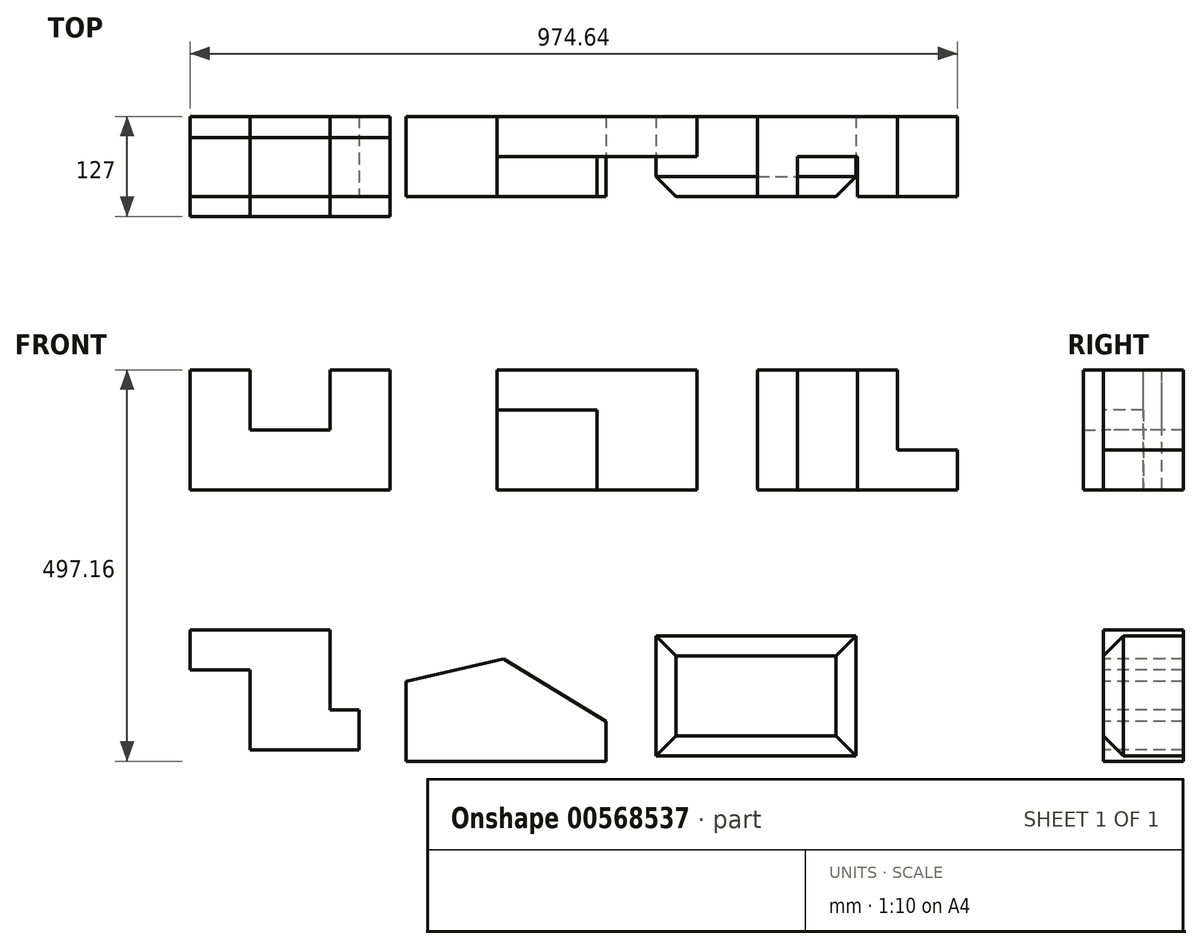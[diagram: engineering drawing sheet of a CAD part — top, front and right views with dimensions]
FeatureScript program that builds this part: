
annotation { "Feature Type Name" : "Feature", "Feature Type Description" : "" }
export const myFeature = defineFeature(function(context is Context, id is Id, definition is map)
    precondition{}
    {
        {
            var Q0;
            Q0=qCreatedBy(makeId("Front.planeOp"),FACE);
            var sketch = newSketch(context, id + "F0", { "sketchPlane" : qUnion([Q0])});
            skLineSegment(sketch, "E0", {"start": v(0, 0) * mm, "end": v(0, 152.4) * mm});
            skLineSegment(sketch, "E1", {"start": v(0, 152.4) * mm, "end": v(76.2, 152.4) * mm});
            skLineSegment(sketch, "E2", {"start": v(76.2, 152.4) * mm, "end": v(76.2, 76.2) * mm});
            skLineSegment(sketch, "E3", {"start": v(76.2, 76.2) * mm, "end": v(177.8, 76.2) * mm});
            skLineSegment(sketch, "E4", {"start": v(177.8, 76.2) * mm, "end": v(177.8, 152.4) * mm});
            skLineSegment(sketch, "E5", {"start": v(177.8, 152.4) * mm, "end": v(254, 152.4) * mm});
            skLineSegment(sketch, "E6", {"start": v(254, 152.4) * mm, "end": v(254, 0) * mm});
            skLineSegment(sketch, "E7", {"start": v(254, 0) * mm, "end": v(0, 0) * mm});
            skSolve(sketch);
        }
        {
            var Q0;
            Q0=makeQuery(id+"F0.imprint","IMPRINT",FACE,{"disambiguationData":[TD([[makeQuery(id+"F0.imprint","IMPRINT",EDGE,{"derivedFrom":sQuery(id+"F0.wireOp",EDGE,"E0")}),-1.0]])]});
            extrude(context, id + "F1", {"entities" : qUnion([Q0]), "oppositeDirection" : true, "depth" : 101.6 * mm, "offsetDistance" : 25.4 * mm});
        }
        {
            var Q0;
            Q0=qCreatedBy(makeId("Front.planeOp"),FACE);
            var sketch = newSketch(context, id + "F2", { "sketchPlane" : qUnion([Q0])});
            skLineSegment(sketch, "E8.bottom", {"start": v(390.09, 0) * mm, "end": v(644.09, 0) * mm});
            skLineSegment(sketch, "E8.top", {"start": v(390.09, 152.4) * mm, "end": v(644.09, 152.4) * mm});
            skLineSegment(sketch, "E8.left", {"start": v(390.09, 0) * mm, "end": v(390.09, 152.4) * mm});
            skLineSegment(sketch, "E8.right", {"start": v(644.09, 0) * mm, "end": v(644.09, 152.4) * mm});
            skSolve(sketch);
        }
        {
            var Q0;
            Q0=makeQuery(id+"F2.imprint","IMPRINT",FACE,{"disambiguationData":[TD([[makeQuery(id+"F2.imprint","IMPRINT",EDGE,{"derivedFrom":sQuery(id+"F2.wireOp",EDGE,"E8.bottom")}),1.0]])]});
            extrude(context, id + "F3", {"entities" : qUnion([Q0]), "oppositeDirection" : true, "depth" : 101.6 * mm, "offsetDistance" : 25.4 * mm});
        }
        {
            var Q0;
            Q0=makeQuery(id+"F3.opExtrude","CAP_FACE",FACE,{"disambiguationData":[OSD([sQuery(id+"F2.wireOp",EDGE,"E8.bottom"),sQuery(id+"F2.wireOp",EDGE,"E8.top"),sQuery(id+"F2.wireOp",EDGE,"E8.left"),sQuery(id+"F2.wireOp",EDGE,"E8.right")])],"isStart":true});
            var sketch = newSketch(context, id + "F4", { "sketchPlane" : qUnion([Q0])});
            skLineSegment(sketch, "E9", {"start": v(390.09, 152.4) * mm, "end": v(390.09, 101.6) * mm});
            skLineSegment(sketch, "E10", {"start": v(390.09, 101.6) * mm, "end": v(517.09, 101.6) * mm});
            skLineSegment(sketch, "E11", {"start": v(517.09, 101.6) * mm, "end": v(517.09, 0) * mm});
            skLineSegment(sketch, "E12", {"start": v(517.09, 0) * mm, "end": v(644.09, 0) * mm});
            skLineSegment(sketch, "E13", {"start": v(644.09, 0) * mm, "end": v(644.09, 152.4) * mm});
            skLineSegment(sketch, "E14", {"start": v(644.09, 152.4) * mm, "end": v(390.09, 152.4) * mm});
            skSolve(sketch);
        }
        {
            var Q0;
            Q0=makeQuery(id+"F4.imprint","IMPRINT",FACE,{"disambiguationData":[TD([[makeQuery(id+"F4.imprint","IMPRINT",EDGE,{"derivedFrom":sQuery(id+"F4.wireOp",EDGE,"E9")}),-1.0]])]});
            extrude(context, id + "F5", {"entities" : qUnion([Q0]), "operationType" : NewBodyOperationType.REMOVE, "oppositeDirection" : true, "depth" : 50.8 * mm, "offsetDistance" : 25.4 * mm});
        }
        {
            var Q0;
            Q0=qCreatedBy(makeId("Front.planeOp"),FACE);
            var sketch = newSketch(context, id + "F6", { "sketchPlane" : qUnion([Q0])});
            skLineSegment(sketch, "E15", {"start": v(720.64, 0) * mm, "end": v(720.64, 152.4) * mm});
            skLineSegment(sketch, "E16", {"start": v(720.64, 152.4) * mm, "end": v(898.44, 152.4) * mm});
            skLineSegment(sketch, "E17", {"start": v(898.44, 152.4) * mm, "end": v(898.44, 50.8) * mm});
            skLineSegment(sketch, "E18", {"start": v(898.44, 50.8) * mm, "end": v(974.64, 50.8) * mm});
            skLineSegment(sketch, "E19", {"start": v(974.64, 50.8) * mm, "end": v(974.64, 0) * mm});
            skLineSegment(sketch, "E20", {"start": v(974.64, 0) * mm, "end": v(720.64, 0) * mm});
            skSolve(sketch);
        }
        {
            var Q0;
            Q0=makeQuery(id+"F6.imprint","IMPRINT",FACE,{"disambiguationData":[TD([[makeQuery(id+"F6.imprint","IMPRINT",EDGE,{"derivedFrom":sQuery(id+"F6.wireOp",EDGE,"E15")}),-1.0]])]});
            extrude(context, id + "F7", {"entities" : qUnion([Q0]), "oppositeDirection" : true, "depth" : 101.6 * mm, "offsetDistance" : 25.4 * mm});
        }
        {
            var Q0;
            Q0=makeQuery(id+"F7.opExtrude","SWEPT_FACE",FACE,{"disambiguationData":[OSD([sQuery(id+"F6.wireOp",EDGE,"E16")])]});
            var sketch = newSketch(context, id + "F8", { "sketchPlane" : qUnion([Q0])});
            skLineSegment(sketch, "E21.bottom", {"start": v(771.44, 50.8) * mm, "end": v(847.64, 50.8) * mm});
            skLineSegment(sketch, "E21.right", {"start": v(847.64, 50.8) * mm, "end": v(847.64, 0) * mm});
            skLineSegment(sketch, "E22", {"start": v(771.44, 50.8) * mm, "end": v(771.44, 0) * mm});
            skLineSegment(sketch, "E23", {"start": v(771.44, 0) * mm, "end": v(847.64, 0) * mm});
            skSolve(sketch);
        }
        {
            var Q0;
            Q0=makeQuery(id+"F8.imprint","IMPRINT",FACE,{"disambiguationData":[TD([[makeQuery(id+"F8.imprint","IMPRINT",EDGE,{"derivedFrom":sQuery(id+"F8.wireOp",EDGE,"E21.bottom")}),-1.0]])]});
            extrude(context, id + "F9", {"entities" : qUnion([Q0]), "operationType" : NewBodyOperationType.REMOVE, "oppositeDirection" : true, "depth" : 152.4 * mm, "offsetDistance" : 25.4 * mm});
        }
        {
            var Q0;
            Q0=qCreatedBy(makeId("Front.planeOp"),FACE);
            var sketch = newSketch(context, id + "F10", { "sketchPlane" : qUnion([Q0])});
            skLineSegment(sketch, "E24", {"start": v(0, -177.8) * mm, "end": v(177.8, -177.8) * mm});
            skLineSegment(sketch, "E25", {"start": v(177.8, -177.8) * mm, "end": v(177.8, -279.4) * mm});
            skLineSegment(sketch, "E26", {"start": v(177.8, -279.4) * mm, "end": v(214.3, -279.4) * mm});
            skLineSegment(sketch, "E27", {"start": v(214.3, -279.4) * mm, "end": v(214.3, -330.2) * mm});
            skLineSegment(sketch, "E28", {"start": v(214.3, -330.2) * mm, "end": v(76.2, -330.2) * mm});
            skLineSegment(sketch, "E29", {"start": v(76.2, -330.2) * mm, "end": v(76.2, -228.6) * mm});
            skLineSegment(sketch, "E30", {"start": v(76.2, -228.6) * mm, "end": v(0, -228.6) * mm});
            skLineSegment(sketch, "E31", {"start": v(0, -228.6) * mm, "end": v(0, -177.8) * mm});
            skSolve(sketch);
        }
        {
            var Q0;
            Q0 = qSketchRegion(id + "F10", true);
            extrude(context, id + "F11", {"entities" : qUnion([Q0]), "oppositeDirection" : true, "depth" : 101.6 * mm, "offsetDistance" : 25.4 * mm});
        }
        {
            var Q0;
            Q0=qCreatedBy(makeId("Front.planeOp"),FACE);
            var sketch = newSketch(context, id + "F12", { "sketchPlane" : qUnion([Q0])});
            skLineSegment(sketch, "E32", {"start": v(274.07, -344.76) * mm, "end": v(274.07, -243.16) * mm});
            skLineSegment(sketch, "E33", {"start": v(274.07, -243.16) * mm, "end": v(397.86, -214.77) * mm});
            skLineSegment(sketch, "E34", {"start": v(397.86, -214.77) * mm, "end": v(528.07, -293.96) * mm});
            skLineSegment(sketch, "E35", {"start": v(528.07, -293.96) * mm, "end": v(528.07, -344.76) * mm});
            skLineSegment(sketch, "E36", {"start": v(528.07, -344.76) * mm, "end": v(274.07, -344.76) * mm});
            skSolve(sketch);
        }
        {
            var Q0;
            Q0=makeQuery(id+"F12.imprint","IMPRINT",FACE,{"disambiguationData":[TD([[makeQuery(id+"F12.imprint","IMPRINT",EDGE,{"derivedFrom":sQuery(id+"F12.wireOp",EDGE,"E32")}),-1.0]])]});
            extrude(context, id + "F13", {"entities" : qUnion([Q0]), "oppositeDirection" : true, "depth" : 101.6 * mm, "offsetDistance" : 25.4 * mm});
        }
        {
            var Q0;
            Q0=qCreatedBy(makeId("Front.planeOp"),FACE);
            var sketch = newSketch(context, id + "F14", { "sketchPlane" : qUnion([Q0])});
            skLineSegment(sketch, "E37.bottom", {"start": v(591.6, -337.96) * mm, "end": v(845.6, -337.96) * mm});
            skLineSegment(sketch, "E37.top", {"start": v(591.6, -185.56) * mm, "end": v(845.6, -185.56) * mm});
            skLineSegment(sketch, "E37.left", {"start": v(591.6, -337.96) * mm, "end": v(591.6, -185.56) * mm});
            skLineSegment(sketch, "E37.right", {"start": v(845.6, -337.96) * mm, "end": v(845.6, -185.56) * mm});
            skSolve(sketch);
        }
        {
            var Q0;
            Q0=makeQuery(id+"F14.imprint","IMPRINT",FACE,{"disambiguationData":[TD([[makeQuery(id+"F14.imprint","IMPRINT",EDGE,{"derivedFrom":sQuery(id+"F14.wireOp",EDGE,"E37.bottom")}),1.0]])]});
            extrude(context, id + "F15", {"entities" : qUnion([Q0]), "oppositeDirection" : true, "depth" : 101.6 * mm, "offsetDistance" : 25.4 * mm});
        }
        {
            var Q0;
            Q0=makeQuery(id+"F15.opExtrude","CAP_FACE",FACE,{"disambiguationData":[OSD([sQuery(id+"F14.wireOp",EDGE,"E37.bottom"),sQuery(id+"F14.wireOp",EDGE,"E37.top"),sQuery(id+"F14.wireOp",EDGE,"E37.left"),sQuery(id+"F14.wireOp",EDGE,"E37.right")])],"isStart":true});
            chamfer(context, id + "F16", {"entities" : qUnion([Q0]), "width" : 25.4 * mm, "tangentPropagation" : true});
        }
        {
            var Q0;
            Q0 = qSketchRegion(id + "F0", true);
            extrude(context, id + "F17", {"entities" : qUnion([Q0]), "depth" : 25.4 * mm, "offsetDistance" : 25.4 * mm});
        }
        {
            var Q0;
            Q0 = qSketchRegion(id + "F0", true);
            extrude(context, id + "F18", {"entities" : qUnion([Q0]), "oppositeDirection" : true, "depth" : 74.68 * mm, "offsetDistance" : 25.4 * mm});
        }
    });
